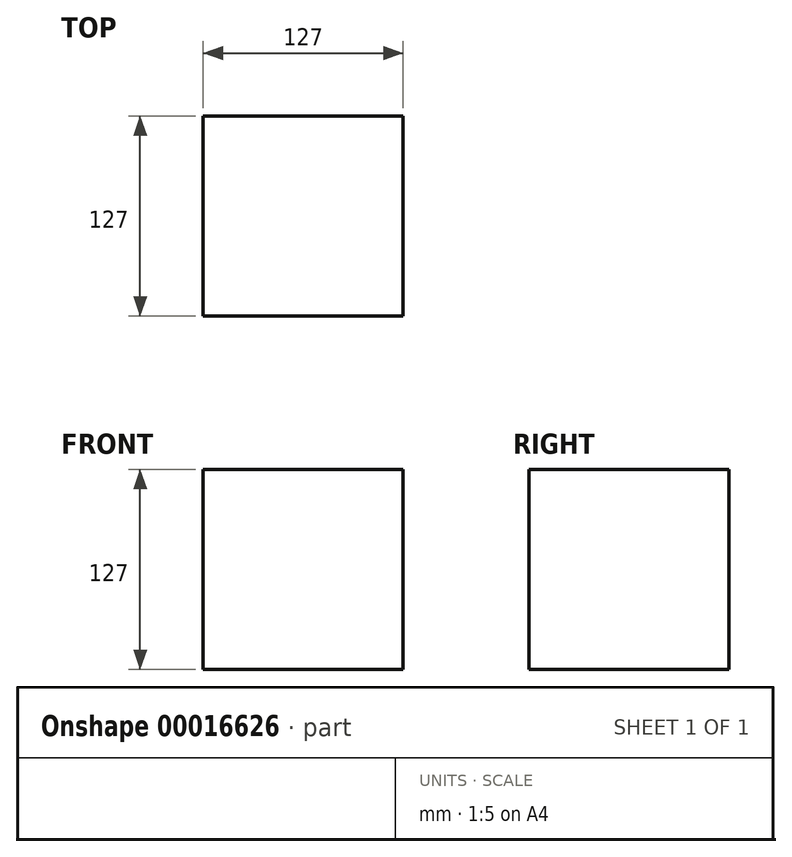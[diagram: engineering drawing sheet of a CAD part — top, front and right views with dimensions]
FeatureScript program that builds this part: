
annotation { "Feature Type Name" : "Feature", "Feature Type Description" : "" }
export const myFeature = defineFeature(function(context is Context, id is Id, definition is map)
    precondition{}
    {
        {
            var Q0;
            Q0=qCreatedBy(makeId("Top.planeOp"),FACE);
            var sketch = newSketch(context, id + "F0", { "sketchPlane" : qUnion([Q0])});
            skLineSegment(sketch, "E0.bottom", {"start": v(0, 0) * mm, "end": v(127, 0) * mm});
            skLineSegment(sketch, "E0.top", {"start": v(0, -127) * mm, "end": v(127, -127) * mm});
            skLineSegment(sketch, "E0.left", {"start": v(0, 0) * mm, "end": v(0, -127) * mm});
            skLineSegment(sketch, "E0.right", {"start": v(127, 0) * mm, "end": v(127, -127) * mm});
            skSolve(sketch);
        }
        {
            var Q0;
            Q0=sQuery(id+"F0.wireOp",EDGE,"E0.left");
            var Q1;
            Q1=sQuery(id+"F0.wireOp",EDGE,"E0.bottom");
            var Q2;
            Q2=sQuery(id+"F0.wireOp",EDGE,"E0.right");
            var Q3;
            Q3=sQuery(id+"F0.wireOp",EDGE,"E0.top");
            extrude(context, id + "F1", {"bodyType" : ToolBodyType.SURFACE, "surfaceEntities" : qUnion([Q0, Q1, Q2, Q3]), "depth" : 127 * mm});
        }
    });
